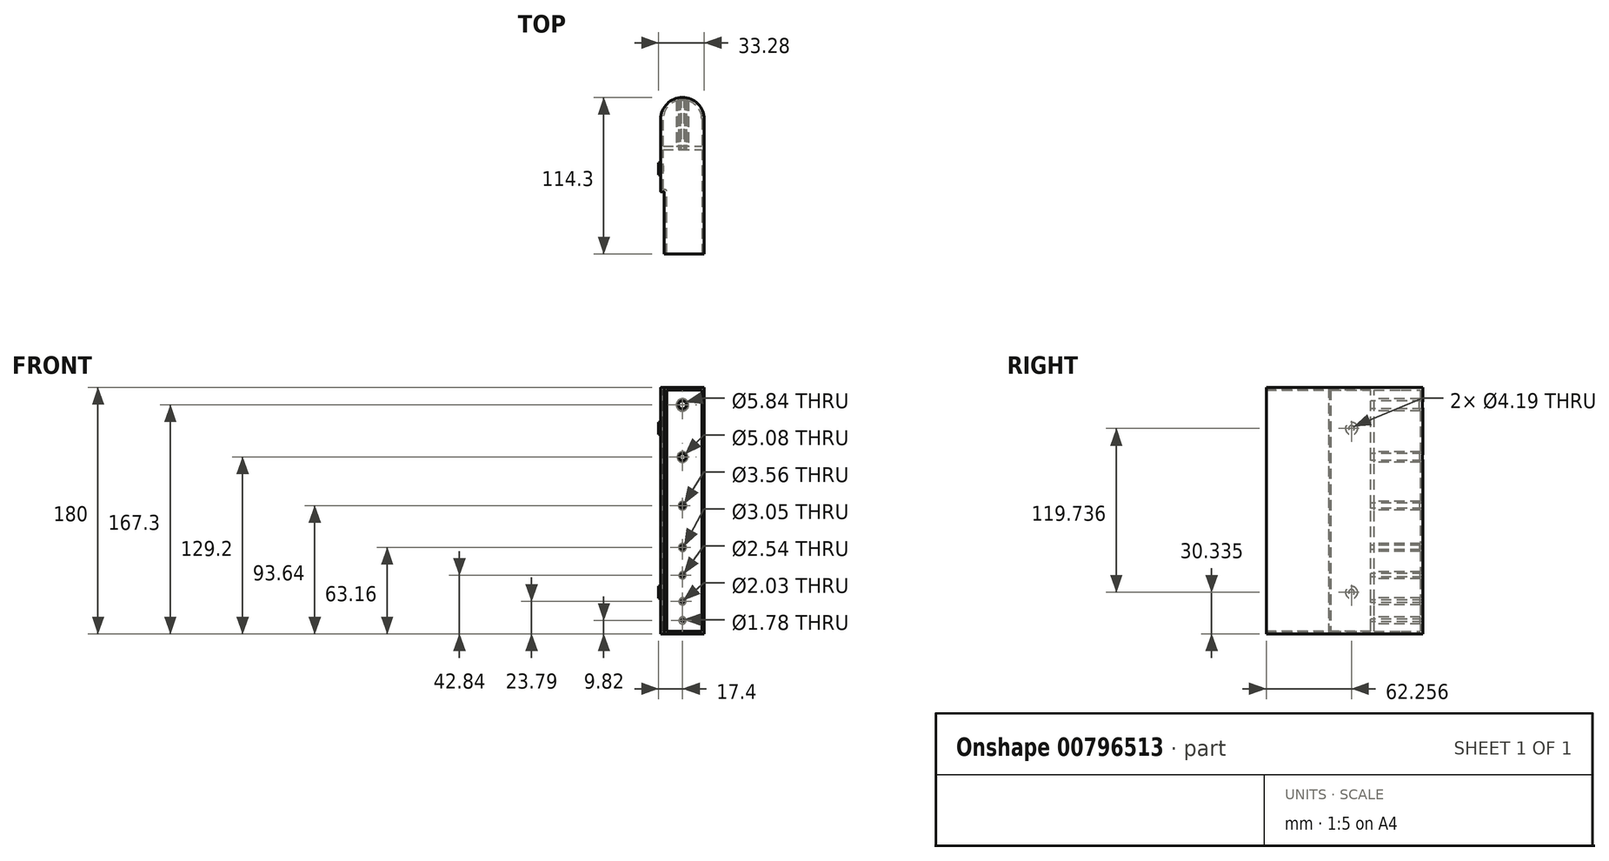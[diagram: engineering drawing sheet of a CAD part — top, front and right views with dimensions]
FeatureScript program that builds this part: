
annotation { "Feature Type Name" : "Feature", "Feature Type Description" : "" }
export const myFeature = defineFeature(function(context is Context, id is Id, definition is map)
    precondition{}
    {
        {
            var Q0;
            Q0=qCreatedBy(makeId("Top.planeOp"),FACE);
            var sketch = newSketch(context, id + "F0", { "sketchPlane" : qUnion([Q0])});
            skLineSegment(sketch, "E0", {"start": v(-13.33, -45.34) * mm, "end": v(-13.33, 0) * mm});
            skLineSegment(sketch, "E1", {"start": v(-13.35, 0) * mm, "end": v(-15.5, 0) * mm});
            skLineSegment(sketch, "E2", {"start": v(-15.87, 0.38) * mm, "end": v(-15.87, 53.09) * mm});
            skArc(sketch, "E3", {"start": v(15.88, 53.09) * mm, "mid": v(0, 68.96) * mm, "end": v(-15.87, 53.09) * mm});
            skLineSegment(sketch, "E4", {"start": v(15.88, 53.09) * mm, "end": v(15.88, -45.34) * mm});
            skLineSegment(sketch, "E5", {"start": v(15.87, -45.34) * mm, "end": v(-13.33, -45.34) * mm});
            skPoint(sketch, "E6.visualSharp", {"position": v(-15.88, 0) * mm});
            skArc(sketch, "E6.filletArc", {"start": v(-15.87, 0.38) * mm, "mid": v(-15.76, 0.11) * mm, "end": v(-15.5, 0) * mm});
            skPoint(sketch, "E7.visualSharp", {"position": v(0, 0) * mm});
            skArc(sketch, "E7.filletArc", {"start": v(-13.33, 0) * mm, "mid": v(-13.34, 0) * mm, "end": v(-13.35, 0) * mm});
            skSolve(sketch);
        }
        {
            var Q0;
            Q0=makeQuery(id+"F0.imprint","IMPRINT",FACE,{"disambiguationData":[TD([[makeQuery(id+"F0.imprint","IMPRINT",EDGE,{"derivedFrom":sQuery(id+"F0.wireOp",EDGE,"E0")}),-1.0]])]});
            extrude(context, id + "F1", {"entities" : qUnion([Q0]), "endBound" : BoundingType.SYMMETRIC, "depth" : 180 * mm, "offsetDistance" : 25.4 * mm});
        }
        {
            var Q0;
            Q0=makeQuery(id+"F1.opExtrude","SWEPT_FACE",FACE,{"disambiguationData":[OSD([sQuery(id+"F0.wireOp",EDGE,"E5")])]});
            shell(context, id + "F2", {"entities" : qUnion([Q0]), "thickness" : 1.78 * mm});
        }
        {
            var Q0;
            Q0=qCreatedBy(makeId("Front.planeOp"),FACE);
            cPlane(context, id + "F3", {"entities" : qUnion([Q0]), "cplaneType" : CPlaneType.OFFSET, "offset" : 68.96 * mm, "oppositeDirection" : true, "width" : 152.4 * mm, "height" : 152.4 * mm});
        }
        {
            var Q0;
            Q0=makeQuery(id+"F1.opExtrude","SWEPT_FACE",FACE,{"disambiguationData":[OSD([sQuery(id+"F0.wireOp",EDGE,"E2")])]});
            cPlane(context, id + "F4", {"entities" : qUnion([Q0]), "cplaneType" : CPlaneType.OFFSET, "offset" : 0 * mm, "width" : 152.4 * mm, "height" : 152.4 * mm});
        }
        {
            var Q0;
            Q0=qCreatedBy(id+"F4.planeOp",FACE);
            var sketch = newSketch(context, id + "F5", { "sketchPlane" : qUnion([Q0])});
            skCircle(sketch, "E8", {"center": v(-16.92, 60.07) * mm, "radius": 4.45 * mm});
            skCircle(sketch, "E9", {"center": v(-16.92, -59.66) * mm, "radius": 4.45 * mm});
            skCircle(sketch, "E10", {"center": v(-16.92, -59.66) * mm, "radius": 2.1 * mm});
            skCircle(sketch, "E11", {"center": v(-16.92, 60.07) * mm, "radius": 2.1 * mm});
            skSolve(sketch);
        }
        {
            var Q0;
            Q0=makeQuery(id+"F5.imprint","IMPRINT",FACE,{"disambiguationData":[TD([[makeQuery(id+"F5.imprint","IMPRINT",EDGE,{"derivedFrom":sQuery(id+"F5.wireOp",EDGE,"E9")}),1.0]])]});
            var Q1;
            Q1=makeQuery(id+"F5.imprint","IMPRINT",FACE,{"disambiguationData":[TD([[makeQuery(id+"F5.imprint","IMPRINT",EDGE,{"derivedFrom":sQuery(id+"F5.wireOp",EDGE,"E8")}),1.0]])]});
            extrude(context, id + "F6", {"entities" : qUnion([Q0, Q1]), "operationType" : NewBodyOperationType.ADD, "depth" : 1.52 * mm, "offsetDistance" : 25.4 * mm});
        }
        {
            var Q0;
            Q0=makeQuery(id+"F6.boolean.opBoolean","SPLIT",FACE,{"disambiguationData":[TD([makeQuery(id+"F6.opExtrude","SWEPT_FACE",FACE,{"disambiguationData":[OSD([sQuery(id+"F5.wireOp",EDGE,"E10")])]})])],"derivedFrom":makeQuery(id+"F1.opExtrude","SWEPT_FACE",FACE,{"disambiguationData":[OSD([sQuery(id+"F0.wireOp",EDGE,"E2")])]})});
            var Q1;
            Q1=makeQuery(id+"F6.boolean.opBoolean","SPLIT",FACE,{"disambiguationData":[TD([makeQuery(id+"F6.opExtrude","SWEPT_FACE",FACE,{"disambiguationData":[OSD([sQuery(id+"F5.wireOp",EDGE,"E11")])]})])],"derivedFrom":makeQuery(id+"F1.opExtrude","SWEPT_FACE",FACE,{"disambiguationData":[OSD([sQuery(id+"F0.wireOp",EDGE,"E2")])]})});
            extrude(context, id + "F7", {"entities" : qUnion([Q0, Q1]), "operationType" : NewBodyOperationType.REMOVE, "oppositeDirection" : true, "depth" : 25.4 * mm, "offsetDistance" : 25.4 * mm});
        }
        {
            var Q0;
            Q0=qCreatedBy(id+"F3.planeOp",FACE);
            cPlane(context, id + "F8", {"entities" : qUnion([Q0]), "cplaneType" : CPlaneType.OFFSET, "offset" : 38.1 * mm, "width" : 152.4 * mm, "height" : 152.4 * mm});
        }
        {
            var Q0;
            Q0=qCreatedBy(id+"F8.planeOp",FACE);
            var sketch = newSketch(context, id + "F9", { "sketchPlane" : qUnion([Q0])});
            skLineSegment(sketch, "E12.bottom", {"start": v(15.88, 90) * mm, "end": v(-15.88, 90) * mm});
            skLineSegment(sketch, "E12.top", {"start": v(15.88, -90) * mm, "end": v(-15.87, -90) * mm});
            skLineSegment(sketch, "E12.left", {"start": v(15.88, 90) * mm, "end": v(15.88, -90) * mm});
            skLineSegment(sketch, "E12.right", {"start": v(-15.88, 90) * mm, "end": v(-15.87, -90) * mm});
            skCircle(sketch, "E13", {"center": v(0, 77.3) * mm, "radius": 2.92 * mm});
            skCircle(sketch, "E14", {"center": v(0, 39.2) * mm, "radius": 2.54 * mm});
            skCircle(sketch, "E15", {"center": v(0, 3.64) * mm, "radius": 1.78 * mm});
            skCircle(sketch, "E16", {"center": v(0, -26.84) * mm, "radius": 1.52 * mm});
            skCircle(sketch, "E17", {"center": v(0, -47.16) * mm, "radius": 1.27 * mm});
            skCircle(sketch, "E18", {"center": v(0, -66.21) * mm, "radius": 1.02 * mm});
            skCircle(sketch, "E19", {"center": v(0, -80.18) * mm, "radius": 0.89 * mm});
            skCircle(sketch, "E20", {"center": v(0, 3.64) * mm, "radius": 3.05 * mm});
            skCircle(sketch, "E21", {"center": v(0, 39.2) * mm, "radius": 3.81 * mm});
            skCircle(sketch, "E22", {"center": v(0, 77.3) * mm, "radius": 4.45 * mm});
            skCircle(sketch, "E23", {"center": v(0, -26.84) * mm, "radius": 2.8 * mm});
            skCircle(sketch, "E24", {"center": v(0, -47.16) * mm, "radius": 2.54 * mm});
            skCircle(sketch, "E25", {"center": v(0, -66.21) * mm, "radius": 2.54 * mm});
            skCircle(sketch, "E26", {"center": v(0, -80.18) * mm, "radius": 2.54 * mm});
            skSolve(sketch);
        }
        {
            var Q0;
            Q0=makeQuery(id+"F9.imprint","IMPRINT",FACE,{"disambiguationData":[TD([[makeQuery(id+"F9.imprint","IMPRINT",EDGE,{"derivedFrom":sQuery(id+"F9.wireOp",EDGE,"E12.bottom")}),1.0]])]});
            extrude(context, id + "F10", {"entities" : qUnion([Q0]), "operationType" : NewBodyOperationType.ADD, "oppositeDirection" : true, "depth" : 2.54 * mm, "offsetDistance" : 25.4 * mm});
        }
        {
            var Q0;
            Q0=makeQuery(id+"F9.imprint","IMPRINT",FACE,{"disambiguationData":[TD([[makeQuery(id+"F9.imprint","IMPRINT",EDGE,{"derivedFrom":sQuery(id+"F9.wireOp",EDGE,"E13")}),-1.0]])]});
            var Q1;
            Q1=makeQuery(id+"F9.imprint","IMPRINT",FACE,{"disambiguationData":[TD([[makeQuery(id+"F9.imprint","IMPRINT",EDGE,{"derivedFrom":sQuery(id+"F9.wireOp",EDGE,"E14")}),-1.0]])]});
            var Q2;
            Q2=makeQuery(id+"F9.imprint","IMPRINT",FACE,{"disambiguationData":[TD([[makeQuery(id+"F9.imprint","IMPRINT",EDGE,{"derivedFrom":sQuery(id+"F9.wireOp",EDGE,"E15")}),-1.0]])]});
            var Q3;
            Q3=makeQuery(id+"F9.imprint","IMPRINT",FACE,{"disambiguationData":[TD([[makeQuery(id+"F9.imprint","IMPRINT",EDGE,{"derivedFrom":sQuery(id+"F9.wireOp",EDGE,"E19")}),-1.0]])]});
            var Q4;
            Q4=makeQuery(id+"F9.imprint","IMPRINT",FACE,{"disambiguationData":[TD([[makeQuery(id+"F9.imprint","IMPRINT",EDGE,{"derivedFrom":sQuery(id+"F9.wireOp",EDGE,"E18")}),-1.0]])]});
            var Q5;
            Q5=makeQuery(id+"F9.imprint","IMPRINT",FACE,{"disambiguationData":[TD([[makeQuery(id+"F9.imprint","IMPRINT",EDGE,{"derivedFrom":sQuery(id+"F9.wireOp",EDGE,"E17")}),-1.0]])]});
            var Q6;
            Q6=makeQuery(id+"F9.imprint","IMPRINT",FACE,{"disambiguationData":[TD([[makeQuery(id+"F9.imprint","IMPRINT",EDGE,{"derivedFrom":sQuery(id+"F9.wireOp",EDGE,"E16")}),-1.0]])]});
            var Q7;
            Q7=makeQuery(id+"F1.opExtrude","SWEPT_FACE",FACE,{"disambiguationData":[OSD([sQuery(id+"F0.wireOp",EDGE,"E3")])]});
            extrude(context, id + "F11", {"entities" : qUnion([Q0, Q1, Q2, Q3, Q4, Q5, Q6]), "operationType" : NewBodyOperationType.ADD, "endBound" : BoundingType.UP_TO_NEXT, "oppositeDirection" : true, "depth" : 25.4 * mm, "endBoundEntityFace" : qUnion([Q7]), "offsetDistance" : 25.4 * mm});
        }
        {
            var Q0;
            Q0=makeQuery(id+"F9.imprint","IMPRINT",FACE,{"disambiguationData":[TD([[makeQuery(id+"F9.imprint","IMPRINT",EDGE,{"derivedFrom":sQuery(id+"F9.wireOp",EDGE,"E15")}),1.0]])]});
            var Q1;
            Q1=makeQuery(id+"F9.imprint","IMPRINT",FACE,{"disambiguationData":[TD([[makeQuery(id+"F9.imprint","IMPRINT",EDGE,{"derivedFrom":sQuery(id+"F9.wireOp",EDGE,"E14")}),1.0]])]});
            var Q2;
            Q2=makeQuery(id+"F9.imprint","IMPRINT",FACE,{"disambiguationData":[TD([[makeQuery(id+"F9.imprint","IMPRINT",EDGE,{"derivedFrom":sQuery(id+"F9.wireOp",EDGE,"E13")}),1.0]])]});
            var Q3;
            Q3=makeQuery(id+"F9.imprint","IMPRINT",FACE,{"disambiguationData":[TD([[makeQuery(id+"F9.imprint","IMPRINT",EDGE,{"derivedFrom":sQuery(id+"F9.wireOp",EDGE,"E17")}),1.0]])]});
            var Q4;
            Q4=makeQuery(id+"F9.imprint","IMPRINT",FACE,{"disambiguationData":[TD([[makeQuery(id+"F9.imprint","IMPRINT",EDGE,{"derivedFrom":sQuery(id+"F9.wireOp",EDGE,"E18")}),1.0]])]});
            var Q5;
            Q5=makeQuery(id+"F9.imprint","IMPRINT",FACE,{"disambiguationData":[TD([[makeQuery(id+"F9.imprint","IMPRINT",EDGE,{"derivedFrom":sQuery(id+"F9.wireOp",EDGE,"E19")}),1.0]])]});
            extrude(context, id + "F12", {"entities" : qUnion([Q0, Q1, Q2, Q3, Q4, Q5]), "operationType" : NewBodyOperationType.REMOVE, "endBound" : BoundingType.THROUGH_ALL, "oppositeDirection" : true, "depth" : 25.4 * mm, "offsetDistance" : 25.4 * mm});
        }
    });
